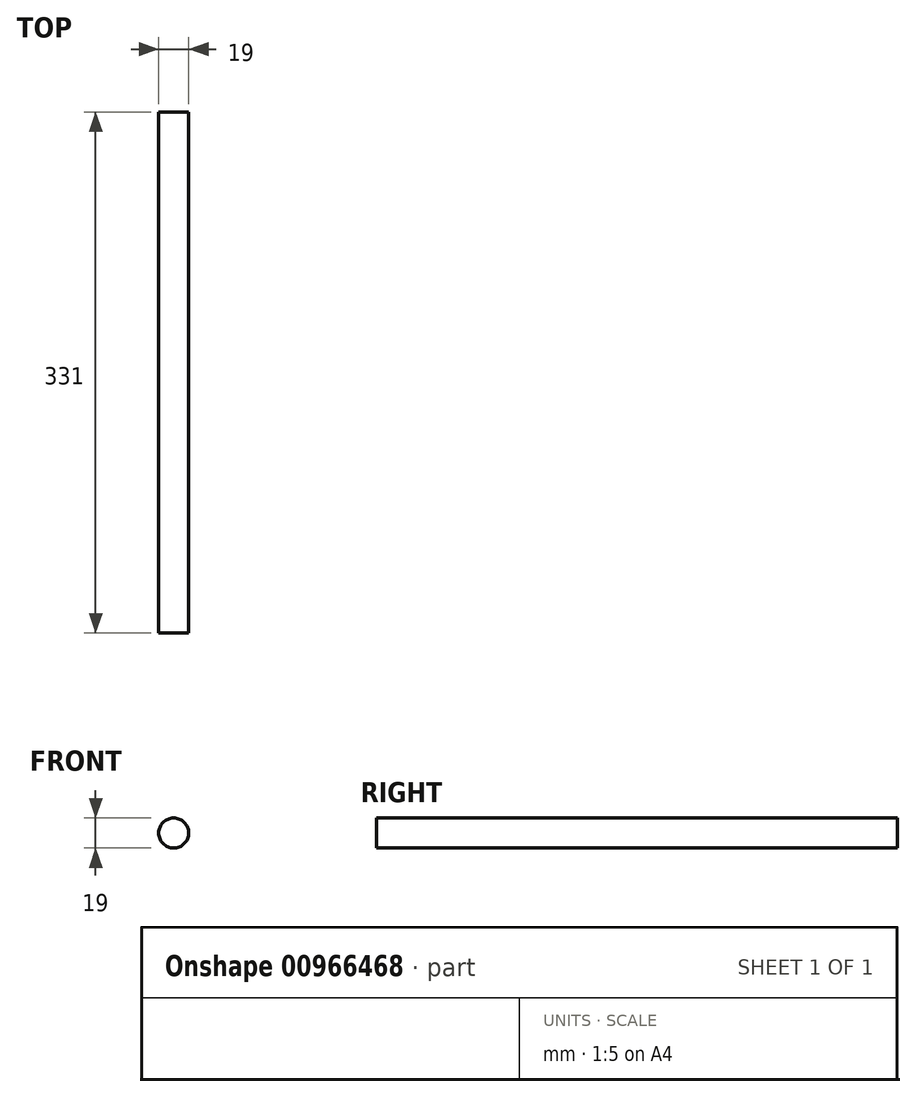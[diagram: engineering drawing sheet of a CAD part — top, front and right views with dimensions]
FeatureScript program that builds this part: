
annotation { "Feature Type Name" : "Feature", "Feature Type Description" : "" }
export const myFeature = defineFeature(function(context is Context, id is Id, definition is map)
    precondition{}
    {
        {
            var Q0;
            Q0=qCreatedBy(makeId("Front.planeOp"),FACE);
            var sketch = newSketch(context, id + "F0", { "sketchPlane" : qUnion([Q0])});
            skCircle(sketch, "E0", {"center": v(0, 0) * mm, "radius": 9.5 * mm});
            skSolve(sketch);
        }
        {
            var Q0;
            Q0=makeQuery(id+"F0.imprint","IMPRINT",FACE,{"disambiguationData":[TD([[makeQuery(id+"F0.imprint","IMPRINT",EDGE,{"derivedFrom":sQuery(id+"F0.wireOp",EDGE,"E0")}),1.0]])]});
            extrude(context, id + "F1", {"entities" : qUnion([Q0]), "depth" : 331 * mm, "offsetDistance" : 25 * mm});
        }
    });
